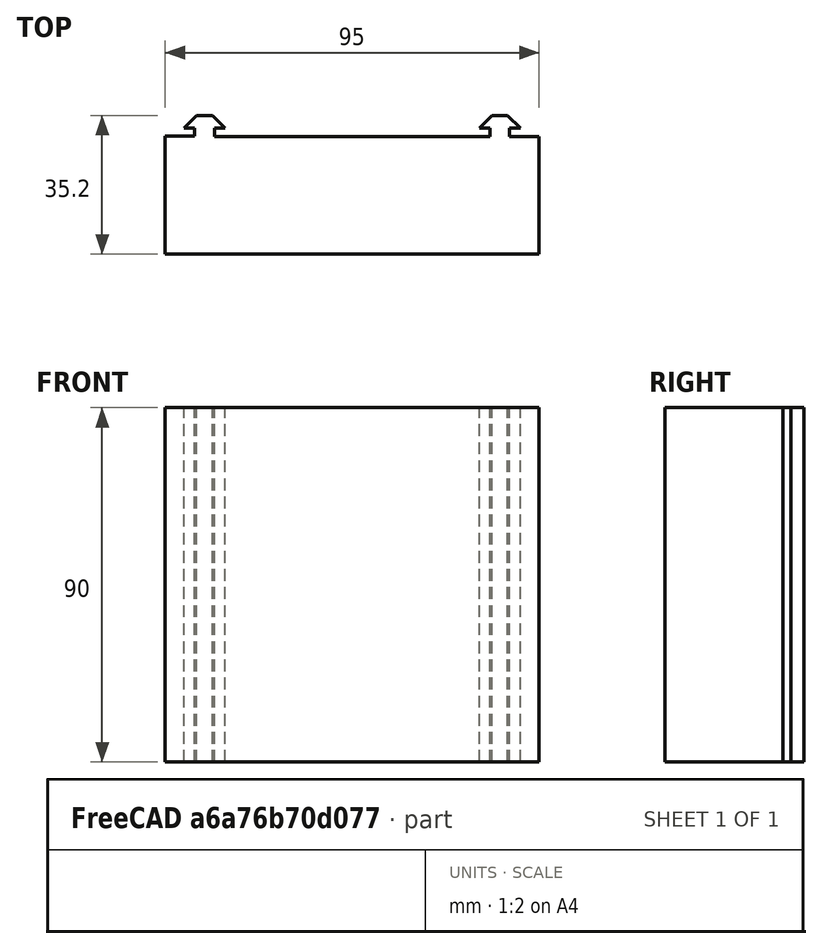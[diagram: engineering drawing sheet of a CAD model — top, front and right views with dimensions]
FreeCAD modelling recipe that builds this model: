
FCSTD DOCUMENT  (FreeCAD 0.18R4 (GitTag))
Label: rainure
License: All rights reserved
LicenseURL: http://en.wikipedia.org/wiki/All_rights_reserved
objects: Sketcher::SketchObject×1, PartDesign::Pad×1, PartDesign::Body×1
note: 4 computed .brp shape members not serialized (recipe doc carries the construction recipe); baked Part::Feature solids carry a one-line shape summary decoded from their .brp

FEATURE [Sketcher::SketchObject] Sketch003
  MapMode = 5
  Placement = pos=(0,0,100) rot=(0,0,1;0rad)
  sketch-geometry (39):
    g0: LineSegment [constr] StartX=13 StartY=-0.5 StartZ=0 EndX=13 EndY=1.5 EndZ=0
    g1: LineSegment [constr] StartX=13 StartY=1.5 StartZ=0 EndX=16 EndY=1.5 EndZ=0
    g2: LineSegment [constr] StartX=16 StartY=1.5 StartZ=0 EndX=12 EndY=5.5 EndZ=0
    g3: LineSegment [constr] StartX=12 StartY=5.5 StartZ=0 EndX=8 EndY=5.5 EndZ=0
    g4: LineSegment [constr] StartX=8 StartY=5.5 StartZ=0 EndX=4 EndY=1.5 EndZ=0
    g5: LineSegment [constr] StartX=4 StartY=1.5 StartZ=0 EndX=7 EndY=1.5 EndZ=0
    g6: LineSegment [constr] StartX=7 StartY=1.5 StartZ=0 EndX=7 EndY=-0.5 EndZ=0
    g7: LineSegment StartX=7.5 StartY=0 StartZ=0 EndX=0 EndY=0 EndZ=0
    g8: LineSegment [constr] StartX=95 StartY=13.1875 StartZ=0 EndX=95 EndY=-40.4075 EndZ=0
    g9: GeomPoint X=47.5 Y=6.34377 Z=0
    g10: LineSegment [constr] StartX=47.5 StartY=30.795 StartZ=0 EndX=47.5 EndY=-44.5049 EndZ=0
    g11: LineSegment [constr] StartX=95 StartY=-0.5 StartZ=0 EndX=95 EndY=-20.0529 EndZ=0
    g12: LineSegment [constr] StartX=95 StartY=-20.0529 StartZ=0 EndX=0 EndY=-20.0529 EndZ=0
    g13: LineSegment StartX=7.5 StartY=0 StartZ=0 EndX=7.5 EndY=2 EndZ=0
    g14: LineSegment StartX=7.5 StartY=2 StartZ=0 EndX=4.8 EndY=2 EndZ=0
    g15: LineSegment StartX=4.8 StartY=2 StartZ=0 EndX=8 EndY=5.2 EndZ=0
    g16: LineSegment StartX=8 StartY=5.2 StartZ=0 EndX=12 EndY=5.2 EndZ=0
    g17: LineSegment StartX=12 StartY=5.2 StartZ=0 EndX=15.2 EndY=2 EndZ=0
    g18: LineSegment StartX=15.2 StartY=2 StartZ=0 EndX=12.5 EndY=2 EndZ=0
    g19: LineSegment StartX=12.5 StartY=2 StartZ=0 EndX=12.5 EndY=-0.086413 EndZ=0
    g20: LineSegment StartX=0 StartY=0 StartZ=0 EndX=0 EndY=-30 EndZ=0
    g21: LineSegment StartX=0 StartY=-30 StartZ=0 EndX=95 EndY=-30 EndZ=0
    g22: LineSegment StartX=95 StartY=-30 StartZ=0 EndX=95 EndY=-0.086413 EndZ=0
    g23: LineSegment [constr] StartX=82 StartY=-0.5 StartZ=0 EndX=82 EndY=1.5 EndZ=0
    g24: LineSegment [constr] StartX=82 StartY=1.5 StartZ=0 EndX=79 EndY=1.5 EndZ=0
    g25: LineSegment [constr] StartX=79 StartY=1.5 StartZ=0 EndX=83 EndY=5.5 EndZ=0
    g26: LineSegment [constr] StartX=83 StartY=5.5 StartZ=0 EndX=87 EndY=5.5 EndZ=0
    g27: LineSegment [constr] StartX=87 StartY=5.5 StartZ=0 EndX=91 EndY=1.5 EndZ=0
    g28: LineSegment [constr] StartX=91 StartY=1.5 StartZ=0 EndX=88 EndY=1.5 EndZ=0
    g29: LineSegment [constr] StartX=88 StartY=1.5 StartZ=0 EndX=88 EndY=-0.5 EndZ=0
    g30: LineSegment StartX=87.5 StartY=-0.086413 StartZ=0 EndX=95 EndY=-0.086413 EndZ=0
    g31: LineSegment StartX=87.5 StartY=-0.086413 StartZ=0 EndX=87.5 EndY=2 EndZ=0
    g32: LineSegment StartX=87.5 StartY=2 StartZ=0 EndX=90.2 EndY=2 EndZ=0
    g33: LineSegment StartX=90.2 StartY=2 StartZ=0 EndX=87 EndY=5.2 EndZ=0
    g34: LineSegment StartX=87 StartY=5.2 StartZ=0 EndX=83 EndY=5.2 EndZ=0
    g35: LineSegment StartX=83 StartY=5.2 StartZ=0 EndX=79.8 EndY=2 EndZ=0
    g36: LineSegment StartX=79.8 StartY=2 StartZ=0 EndX=82.5 EndY=2 EndZ=0
    g37: LineSegment StartX=82.5 StartY=2 StartZ=0 EndX=82.5 EndY=-0.086413 EndZ=0
    g38: LineSegment StartX=82.5 StartY=-0.086413 StartZ=0 EndX=12.5 EndY=-0.086413 EndZ=0
  constraints (76):
    c: Vertical(g8)
    c: Vertical(g10)
    c: PointOnObject(g9,g10)
    c: Vertical(g11)
    c: Block(g11)
    c: Coincident(g13,g14)
    c: Coincident(g14,g15)
    c: Coincident(g15,g16)
    c: Coincident(g16,g17)
    c: Coincident(g17,g18)
    c: Coincident(g18,g19)
    c: Vertical(g13)
    c: Vertical(g19)
    c: Horizontal(g14)
    c: Horizontal(g16)
    c: Horizontal(g18)
    c: Block(g0)
    c: Block(g1)
    c: Block(g2)
    c: Block(g3)
    c: Block(g4)
    c: Block(g5)
    c: Block(g6)
    c: DistanceX(g5,g13) = 0.5
    c: DistanceX(g3,g15) = 0
    c: DistanceX(g18,g0) = 0.5
    c: DistanceY(g5,g13) = 0.5
    c: DistanceY(g15,g3) = 0.3
    c: DistanceY(g0,g18) = 0.5
    c: Parallel(g4,g15)
    c: Parallel(g2,g17)
    c: DistanceX(g16,g2) = 0
    c: Horizontal(g7)
    c: Coincident(g20,g21)
    c: Coincident(g21,g22)
    c: Coincident(g20,g7)
    c: Coincident(g7,g13)
    c: Coincident(g7,g-1)
    c: Vertical(g20)
    c: Vertical(g22)
    c: Horizontal(g21)
    c: Coincident(g31,g32)
    c: Coincident(g32,g33)
    c: Coincident(g33,g34)
    c: Coincident(g34,g35)
    c: Coincident(g35,g36)
    c: Coincident(g36,g37)
    c: Vertical(g31)
    c: Vertical(g37)
    c: Horizontal(g32)
    c: Horizontal(g34)
    c: Horizontal(g36)
    c: Block(g23)
    c: Block(g24)
    c: Block(g25)
    c: Block(g26)
    c: Block(g27)
    c: Block(g28)
    c: Block(g29)
    c: Parallel(g27,g33)
    c: Parallel(g25,g35)
    c: Horizontal(g30)
    c: Coincident(g30,g31)
    c: DistanceY(g20,g7) = 30
    c: PointOnObject(g11,g8)
    c: PointOnObject(g22,g8)
    c: Horizontal(g38)
    c: Block(g37)
    c: Block(g36)
    c: Block(g35)
    c: Block(g34)
    c: Block(g33)
    c: Block(g32)
    c: Block(g31)
    c: Coincident(g38,g37)
    c: Coincident(g38,g19)
FEATURE [PartDesign::Pad] Pad
  Length = 90
  Length2 = 100
  Placement = pos=(0,0,100) rot=(0,0,1;0rad)
  Profile = -> Sketch003
  Type = 0
FEATURE [PartDesign::Body] Body
  Group = -> [Sketch003,Pad]
  Origin = -> Origin
  Tip = -> Pad
